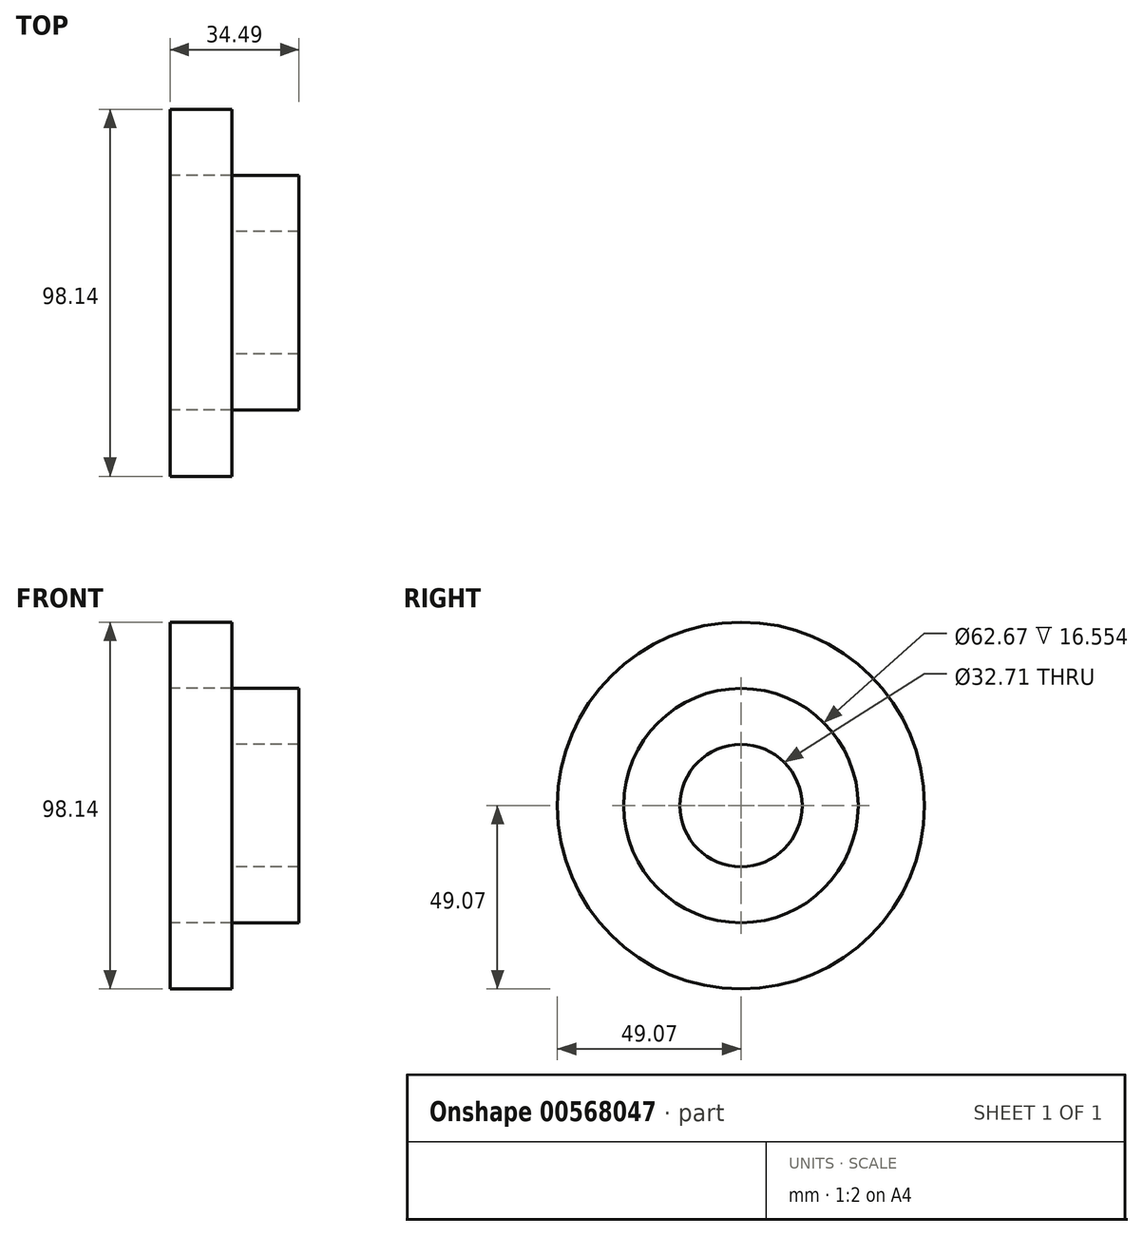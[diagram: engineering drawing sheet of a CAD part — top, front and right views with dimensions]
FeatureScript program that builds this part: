
annotation { "Feature Type Name" : "Feature", "Feature Type Description" : "" }
export const myFeature = defineFeature(function(context is Context, id is Id, definition is map)
    precondition{}
    {
        {
            var Q0;
            Q0=qCreatedBy(makeId("Top.planeOp"),FACE);
            var sketch = newSketch(context, id + "F0", { "sketchPlane" : qUnion([Q0])});
            skLineSegment(sketch, "E0", {"start": v(0, 0) * mm, "end": v(31.73, 0) * mm});
            skLineSegment(sketch, "E1.bottom", {"start": v(0, -16.36) * mm, "end": v(16.55, -16.36) * mm});
            skLineSegment(sketch, "E1.top", {"start": v(0, -49.07) * mm, "end": v(16.55, -49.07) * mm});
            skLineSegment(sketch, "E1.left", {"start": v(0, -16.36) * mm, "end": v(0, -49.07) * mm});
            skLineSegment(sketch, "E1.right", {"start": v(16.55, -16.36) * mm, "end": v(16.55, -49.07) * mm});
            skLineSegment(sketch, "E2.bottom", {"start": v(0, -16.36) * mm, "end": v(34.49, -16.36) * mm});
            skLineSegment(sketch, "E2.top", {"start": v(0, -31.33) * mm, "end": v(34.49, -31.33) * mm});
            skLineSegment(sketch, "E2.left", {"start": v(0, -16.36) * mm, "end": v(0, -31.33) * mm});
            skLineSegment(sketch, "E2.right", {"start": v(34.49, -16.36) * mm, "end": v(34.49, -31.33) * mm});
            skLineSegment(sketch, "E3.MirrorCS", {"start": v(0, 16.36) * mm, "end": v(16.55, 16.36) * mm});
            skLineSegment(sketch, "E4.MirrorCS", {"start": v(34.49, 16.36) * mm, "end": v(34.49, 31.33) * mm});
            skLineSegment(sketch, "E5.MirrorCS", {"start": v(0, 16.36) * mm, "end": v(0, 31.33) * mm});
            skLineSegment(sketch, "E6.MirrorCS", {"start": v(0, 49.07) * mm, "end": v(16.55, 49.07) * mm});
            skLineSegment(sketch, "E7.MirrorCS", {"start": v(0, 16.36) * mm, "end": v(0, 49.07) * mm});
            skLineSegment(sketch, "E8.MirrorCS", {"start": v(16.55, 16.36) * mm, "end": v(16.55, 49.07) * mm});
            skLineSegment(sketch, "E9.MirrorCS", {"start": v(0, 16.36) * mm, "end": v(34.49, 16.36) * mm});
            skLineSegment(sketch, "E10.MirrorCS", {"start": v(0, 31.33) * mm, "end": v(34.49, 31.33) * mm});
            skSolve(sketch);
        }
        {
            var Q0;
            {var subQ0=sQuery(id+"F0.wireOp",EDGE,"E1.top");Q0=makeQuery(id+"F0.imprint","IMPRINT",FACE,{"disambiguationData":[TD([[makeQuery(id+"F0.imprint","IMPRINT",EDGE,{"derivedFrom":subQ0}),1.0]])]});}
            var Q1;
            {var subQ5=sQuery(id+"F0.wireOp",EDGE,"E2.right");Q1=makeQuery(id+"F0.imprint","IMPRINT",FACE,{"disambiguationData":[TD([[makeQuery(id+"F0.imprint","IMPRINT",EDGE,{"derivedFrom":subQ5}),-1.0]])]});}
            var Q2;
            {var subQ5=sQuery(id+"F0.wireOp",EDGE,"E2.left");Q2=makeQuery(id+"F0.imprint","IMPRINT",FACE,{"disambiguationData":[TD([[makeQuery(id+"F0.imprint","IMPRINT",EDGE,{"derivedFrom":subQ5}),1.0]])]});}
            var Q3;
            Q3=sQuery(id+"F0.wireOp",EDGE,"E0");
            revolve(context, id + "F1", {"entities" : qUnion([Q0, Q1, Q2]), "axis" : qUnion([Q3]), "revolveType" : RevolveType.FULL});
        }
    });
